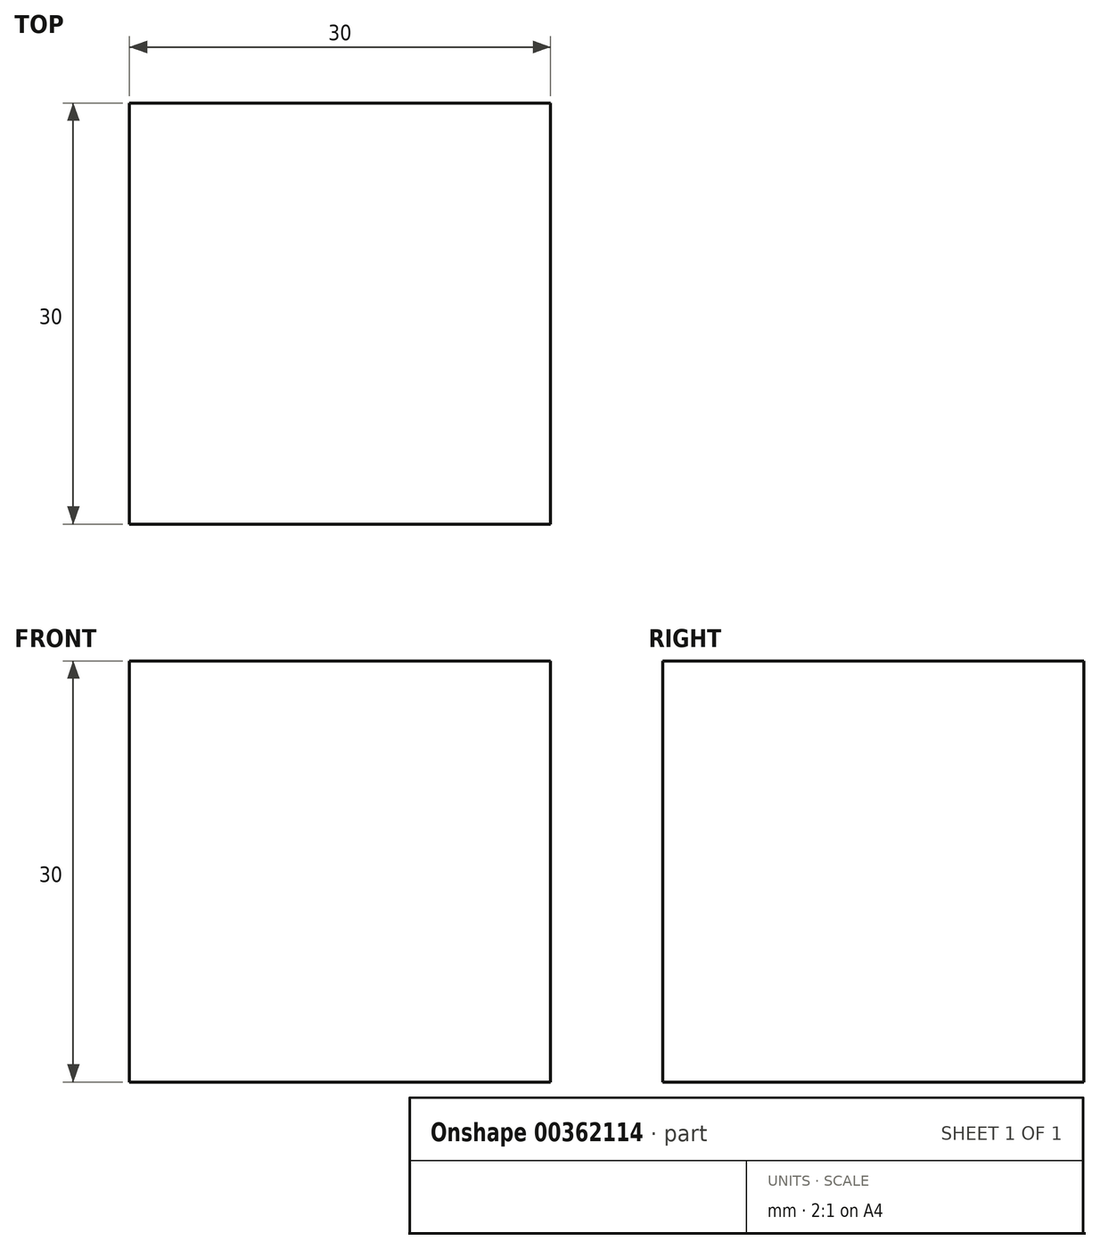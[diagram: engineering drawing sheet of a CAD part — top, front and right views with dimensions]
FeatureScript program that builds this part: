
annotation { "Feature Type Name" : "Feature", "Feature Type Description" : "" }
export const myFeature = defineFeature(function(context is Context, id is Id, definition is map)
    precondition{}
    {
        {
            var Q0;
            Q0=qCreatedBy(makeId("Top.planeOp"),FACE);
            var sketch = newSketch(context, id + "F0", { "sketchPlane" : qUnion([Q0])});
            skLineSegment(sketch, "E0.bottom", {"start": v(15, -15) * mm, "end": v(-15, -15) * mm});
            skLineSegment(sketch, "E0.top", {"start": v(15, 15) * mm, "end": v(-15, 15) * mm});
            skLineSegment(sketch, "E0.left", {"start": v(15, -15) * mm, "end": v(15, 15) * mm});
            skLineSegment(sketch, "E0.right", {"start": v(-15, -15) * mm, "end": v(-15, 15) * mm});
            skPoint(sketch, "E0.middle", {"position": v(0, 0) * mm});
            skSolve(sketch);
        }
        {
            var Q0;
            Q0=makeQuery(id+"F0.imprint","IMPRINT",FACE,{"disambiguationData":[TD([[makeQuery(id+"F0.imprint","IMPRINT",EDGE,{"derivedFrom":sQuery(id+"F0.wireOp",EDGE,"E0.bottom")}),-1.0]])]});
            extrude(context, id + "F1", {"entities" : qUnion([Q0]), "depth" : 30 * mm});
        }
    });
